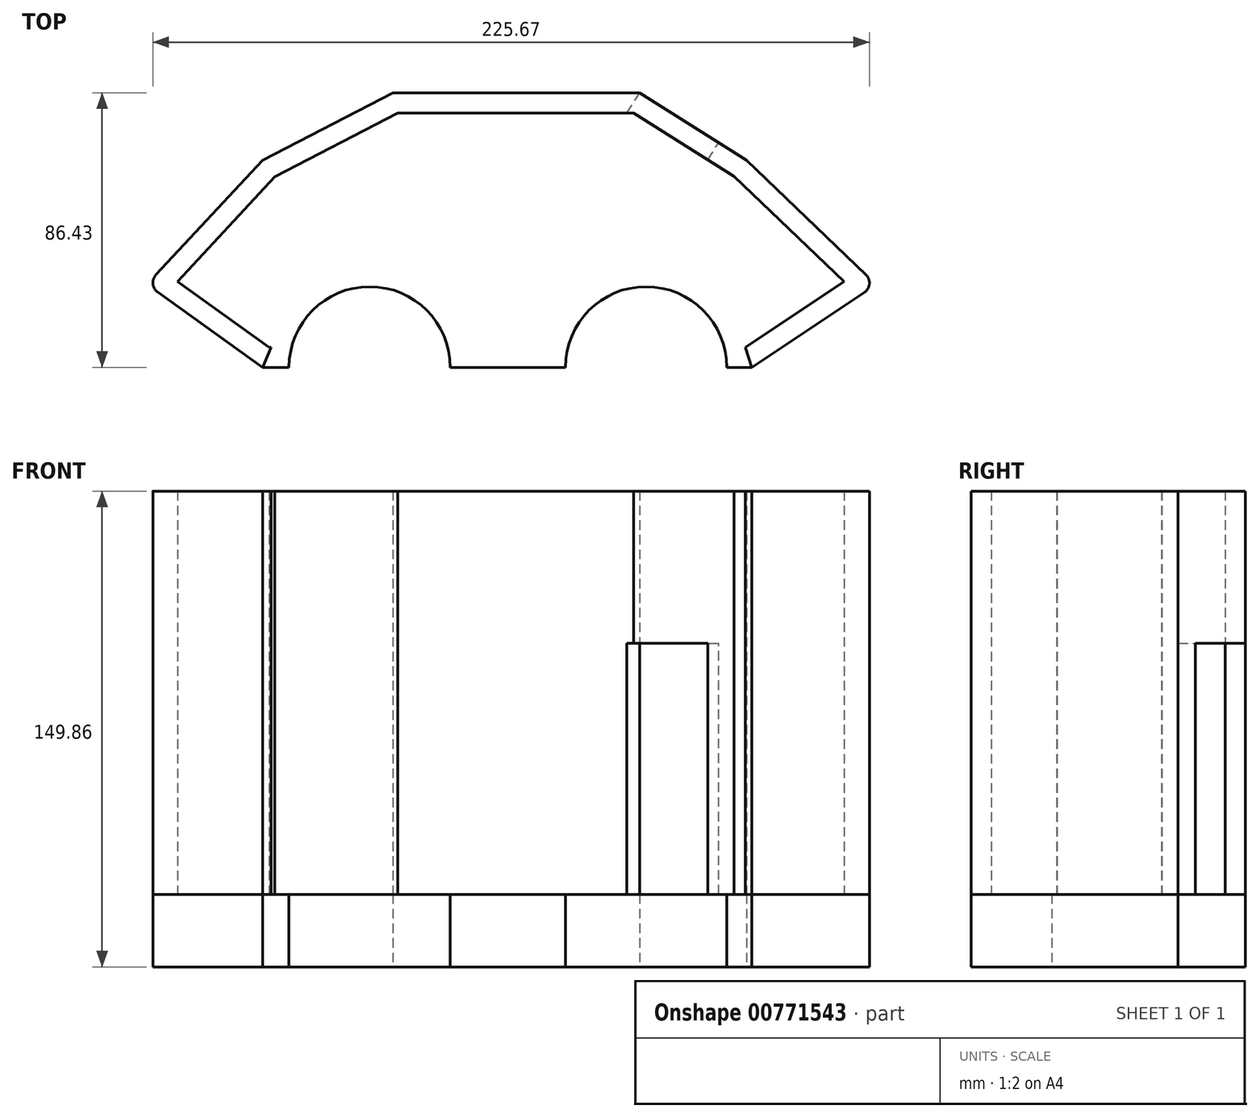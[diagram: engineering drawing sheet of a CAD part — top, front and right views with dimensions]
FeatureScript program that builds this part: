
annotation { "Feature Type Name" : "Feature", "Feature Type Description" : "" }
export const myFeature = defineFeature(function(context is Context, id is Id, definition is map)
    precondition{}
    {
        {
            var Q0;
            Q0=qCreatedBy(makeId("Top.planeOp"),FACE);
            var sketch = newSketch(context, id + "F0", { "sketchPlane" : qUnion([Q0])});
            skLineSegment(sketch, "E0.top", {"start": v(-76.22, -36.04) * mm, "end": v(-67.85, -36.04) * mm});
            skArc(sketch, "E1", {"start": v(-17.05, -36.04) * mm, "mid": v(-42.45, -10.64) * mm, "end": v(-67.85, -36.04) * mm});
            skArc(sketch, "E2", {"start": v(70, -36.04) * mm, "mid": v(44.6, -10.64) * mm, "end": v(19.2, -36.04) * mm});
            skLineSegment(sketch, "E3.trimOffspring", {"start": v(70, -36.04) * mm, "end": v(76.18, -36.04) * mm});
            skLineSegment(sketch, "E4.trimOffspring", {"start": v(-17.05, -36.04) * mm, "end": v(19.2, -36.04) * mm});
            skLineSegment(sketch, "E5", {"start": v(-76.22, -36.04) * mm, "end": v(-109.24, -12.33) * mm});
            skLineSegment(sketch, "E6", {"start": v(-109.78, -6.95) * mm, "end": v(-76.22, 29.14) * mm});
            skLineSegment(sketch, "E7", {"start": v(113.32, -12.44) * mm, "end": v(77.83, -36.04) * mm});
            skLineSegment(sketch, "E8", {"start": v(76.18, 29.14) * mm, "end": v(113.82, -6.83) * mm});
            skLineSegment(sketch, "E9", {"start": v(-76.22, 29.14) * mm, "end": v(-35.14, 50.4) * mm});
            skLineSegment(sketch, "E10", {"start": v(-35.14, 50.4) * mm, "end": v(42.57, 50.4) * mm});
            skLineSegment(sketch, "E11", {"start": v(42.57, 50.4) * mm, "end": v(76.18, 29.14) * mm});
            skPoint(sketch, "E12.visualSharp", {"position": v(-112.56, -9.95) * mm});
            skArc(sketch, "E12.filletArc", {"start": v(-109.78, -6.95) * mm, "mid": v(-110.73, -9.76) * mm, "end": v(-109.24, -12.33) * mm});
            skPoint(sketch, "E13.visualSharp", {"position": v(117.07, -9.95) * mm});
            skArc(sketch, "E13.filletArc", {"start": v(113.32, -12.44) * mm, "mid": v(114.91, -9.76) * mm, "end": v(113.82, -6.83) * mm});
            skLineSegment(sketch, "E14", {"start": v(76.18, -36.04) * mm, "end": v(77.83, -36.04) * mm});
            skSolve(sketch);
        }
        {
            var Q0;
            Q0=makeQuery(id+"F0.imprint","IMPRINT",FACE,{"disambiguationData":[TD([[makeQuery(id+"F0.imprint","IMPRINT",EDGE,{"derivedFrom":sQuery(id+"F0.wireOp",EDGE,"E0.top")}),1.0]])]});
            var Q1;
            Q1 = qSketchRegion(id + "F0", true);
            extrude(context, id + "F1", {"entities" : qUnion([Q0, Q1]), "depth" : 22.86 * mm, "offsetDistance" : 25.4 * mm});
        }
        {
            var Q0;
            Q0=makeQuery(id+"F1.opExtrude","CAP_FACE",FACE,{"disambiguationData":[OSD([sQuery(id+"F0.wireOp",EDGE,"E0.top"),sQuery(id+"F0.wireOp",EDGE,"E1"),sQuery(id+"F0.wireOp",EDGE,"E2"),sQuery(id+"F0.wireOp",EDGE,"E3.trimOffspring"),sQuery(id+"F0.wireOp",EDGE,"E4.trimOffspring"),sQuery(id+"F0.wireOp",EDGE,"E5"),sQuery(id+"F0.wireOp",EDGE,"E6"),sQuery(id+"F0.wireOp",EDGE,"E7"),sQuery(id+"F0.wireOp",EDGE,"E8"),sQuery(id+"F0.wireOp",EDGE,"E9"),sQuery(id+"F0.wireOp",EDGE,"E10"),sQuery(id+"F0.wireOp",EDGE,"E11"),sQuery(id+"F0.wireOp",EDGE,"E12.filletArc"),sQuery(id+"F0.wireOp",EDGE,"E13.filletArc"),sQuery(id+"F0.wireOp",EDGE,"E14")])],"isStart":false});
            var sketch = newSketch(context, id + "F2", { "sketchPlane" : qUnion([Q0])});
            skLineSegment(sketch, "E15", {"start": v(-109.78, -6.95) * mm, "end": v(-76.22, 29.14) * mm});
            skLineSegment(sketch, "E16", {"start": v(-35.14, 50.4) * mm, "end": v(-76.22, 29.14) * mm});
            skLineSegment(sketch, "E17", {"start": v(42.57, 50.4) * mm, "end": v(-35.14, 50.4) * mm});
            skLineSegment(sketch, "E18", {"start": v(76.18, 29.14) * mm, "end": v(113.82, -6.83) * mm});
            skLineSegment(sketch, "E19", {"start": v(113.32, -12.44) * mm, "end": v(77.83, -36.04) * mm});
            skLineSegment(sketch, "E20", {"start": v(-109.24, -12.33) * mm, "end": v(-76.22, -36.04) * mm});
            skLineSegment(sketch, "E21", {"start": v(-76.22, -36.04) * mm, "end": v(-109.24, -12.33) * mm});
            skLineSegment(sketch, "E22.0", {"start": v(75.7, -29.7) * mm, "end": v(75.91, -29.7) * mm});
            skLineSegment(sketch, "E22.1", {"start": v(-33.6, 44.04) * mm, "end": v(-72.32, 24) * mm});
            skLineSegment(sketch, "E22.2", {"start": v(40.73, 44.04) * mm, "end": v(-33.6, 44.04) * mm});
            skLineSegment(sketch, "E22.3", {"start": v(72.25, 24.1) * mm, "end": v(40.73, 44.04) * mm});
            skLineSegment(sketch, "E22.4", {"start": v(106.95, -9.05) * mm, "end": v(72.25, 24.1) * mm});
            skLineSegment(sketch, "E22.5", {"start": v(-72.32, 24) * mm, "end": v(-103, -9) * mm});
            skLineSegment(sketch, "E22.6", {"start": v(75.91, -29.7) * mm, "end": v(106.95, -9.05) * mm});
            skLineSegment(sketch, "E22.7", {"start": v(-103, -9) * mm, "end": v(-74.17, -29.7) * mm});
            skLineSegment(sketch, "E22.8", {"start": v(-74.17, -29.7) * mm, "end": v(-73.56, -29.7) * mm});
            skLineSegment(sketch, "E23", {"start": v(-73.56, -29.7) * mm, "end": v(-76.22, -36.04) * mm});
            skLineSegment(sketch, "E24", {"start": v(75.91, -29.7) * mm, "end": v(77.83, -36.04) * mm});
            skSolve(sketch);
        }
        {
            var Q0;
            Q0=makeQuery(id+"F2.imprint","IMPRINT",FACE,{"disambiguationData":[TD([[makeQuery(id+"F2.imprint","IMPRINT",EDGE,{"derivedFrom":sQuery(id+"F2.wireOp",EDGE,"E15")}),-1.0]])]});
            extrude(context, id + "F3", {"entities" : qUnion([Q0]), "depth" : 127 * mm, "offsetDistance" : 25.4 * mm});
        }
        {
            var Q0;
            Q0=makeQuery(id+"F3.opExtrude","SWEPT_FACE",FACE,{"disambiguationData":[OSD([sQuery(id+"F0.wireOp",EDGE,"E11")])]});
            var sketch = newSketch(context, id + "F4", { "sketchPlane" : qUnion([Q0])});
            skLineSegment(sketch, "E25.bottom", {"start": v(-9.05, 22.86) * mm, "end": v(-38.47, 22.86) * mm});
            skLineSegment(sketch, "E25.top", {"start": v(-9.05, 101.96) * mm, "end": v(-38.47, 101.96) * mm});
            skLineSegment(sketch, "E25.left", {"start": v(-9.05, 22.86) * mm, "end": v(-9.05, 101.96) * mm});
            skLineSegment(sketch, "E25.right", {"start": v(-38.47, 22.86) * mm, "end": v(-38.47, 101.96) * mm});
            skSolve(sketch);
        }
        {
            var Q0;
            Q0 = qSketchRegion(id + "F4", true);
            extrude(context, id + "F5", {"entities" : qUnion([Q0]), "operationType" : NewBodyOperationType.REMOVE, "oppositeDirection" : true, "depth" : 25.4 * mm, "offsetDistance" : 25.4 * mm});
        }
    });
